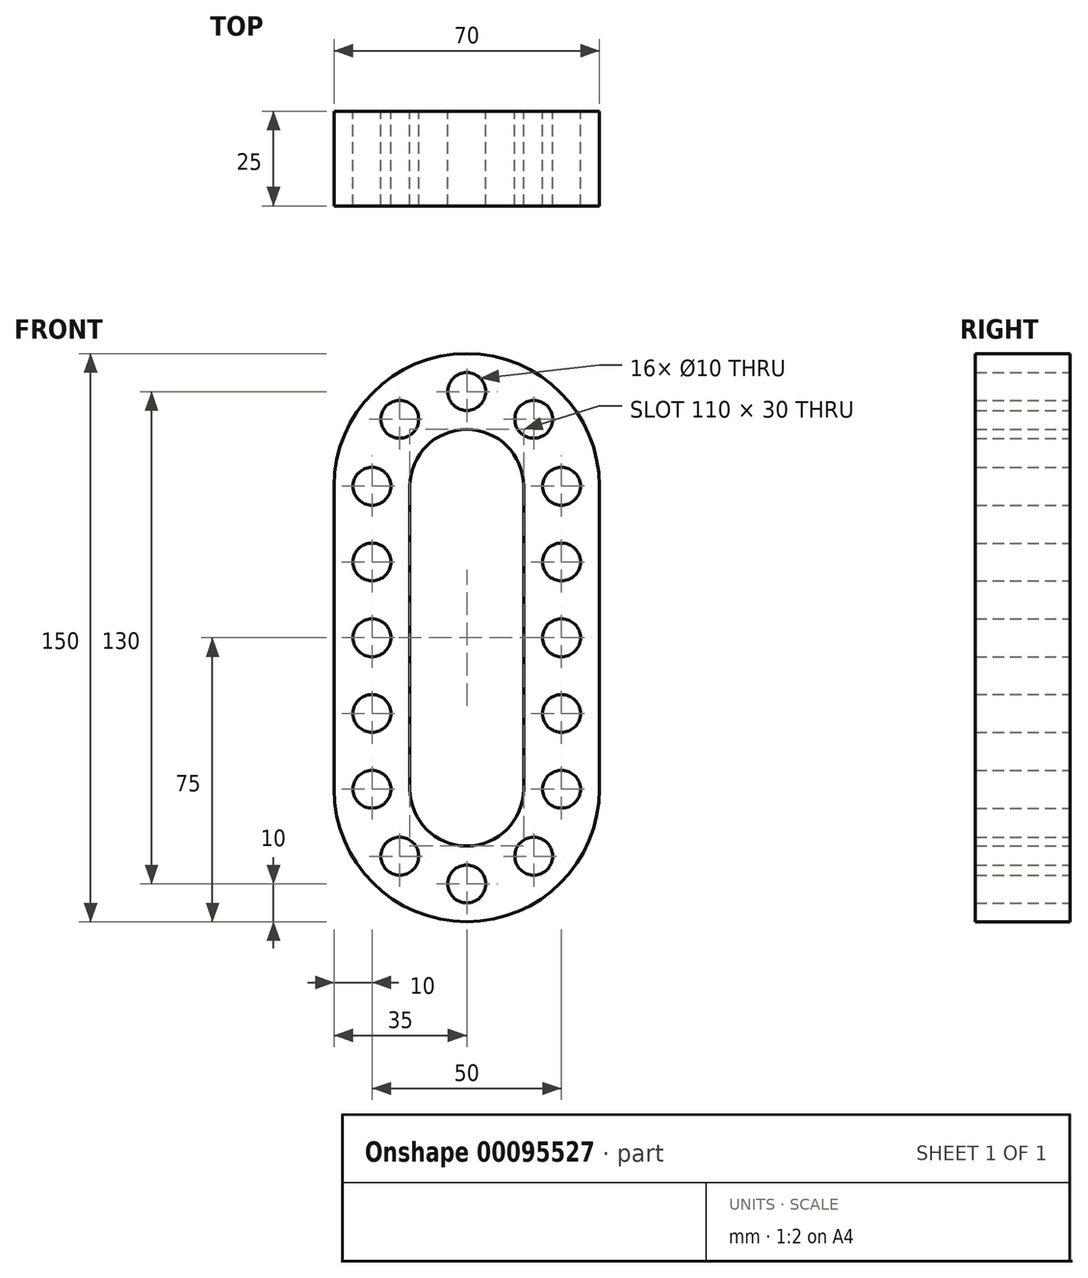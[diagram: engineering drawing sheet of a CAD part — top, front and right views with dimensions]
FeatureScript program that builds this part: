
annotation { "Feature Type Name" : "Feature", "Feature Type Description" : "" }
export const myFeature = defineFeature(function(context is Context, id is Id, definition is map)
    precondition{}
    {
        {
            var Q0;
            Q0=qCreatedBy(makeId("Front.planeOp"),FACE);
            var sketch = newSketch(context, id + "F0", { "sketchPlane" : qUnion([Q0])});
            skPoint(sketch, "E0", {"position": v(-25, 40) * mm});
            skLineSegment(sketch, "E1", {"start": v(-25, 40) * mm, "end": v(-25, 0) * mm, "construction": true});
            skArc(sketch, "E2", {"start": v(0, 65) * mm, "mid": v(-17.68, 57.68) * mm, "end": v(-25, 40) * mm, "construction": true});
            skArc(sketch, "E3.0.startCap", {"start": v(-35, 40) * mm, "mid": v(-25, 50) * mm, "end": v(-15, 40) * mm, "construction": true});
            skLineSegment(sketch, "E3.0.left", {"start": v(-15, 40) * mm, "end": v(-15, 0) * mm});
            skLineSegment(sketch, "E3.0.right", {"start": v(-35, 40) * mm, "end": v(-35, 0) * mm});
            skArc(sketch, "E3.1.startCap", {"start": v(0, 75) * mm, "mid": v(10, 65) * mm, "end": v(0, 55) * mm, "construction": true});
            skArc(sketch, "E3.1.endCap", {"start": v(-15, 40) * mm, "mid": v(-25, 30) * mm, "end": v(-35, 40) * mm, "construction": true});
            skArc(sketch, "E3.1.left", {"start": v(0, 55) * mm, "mid": v(-10.6, 50.6) * mm, "end": v(-15, 40) * mm});
            skArc(sketch, "E3.1.right", {"start": v(0, 75) * mm, "mid": v(-24.75, 64.75) * mm, "end": v(-35, 40) * mm});
            skCircle(sketch, "E4", {"center": v(-25, 40) * mm, "radius": 5 * mm});
            skCircle(sketch, "E5.1.0", {"center": v(-17.68, 57.68) * mm, "radius": 5 * mm});
            skCircle(sketch, "E5.2.0", {"center": v(0, 65) * mm, "radius": 5 * mm});
            skLineSegment(sketch, "E5.anchor1", {"start": v(0, 40) * mm, "end": v(-25, 40) * mm, "construction": true});
            skLineSegment(sketch, "E5.anchor2", {"start": v(0, 40) * mm, "end": v(0, 65) * mm, "construction": true});
            skCircle(sketch, "E6.0.1.0", {"center": v(-25, 20) * mm, "radius": 5 * mm});
            skCircle(sketch, "E6.0.2.0", {"center": v(-25, 0) * mm, "radius": 5 * mm});
            skLineSegment(sketch, "E6.direction1", {"start": v(-25, 40) * mm, "end": v(0, 40) * mm, "construction": true});
            skLineSegment(sketch, "E6.direction2", {"start": v(-25, 40) * mm, "end": v(-25, 20) * mm, "construction": true});
            skLineSegment(sketch, "E7.MirrorCS", {"start": v(0, 40) * mm, "end": v(25, 40) * mm, "construction": true});
            skArc(sketch, "E8.MirrorCS", {"start": v(15, 0) * mm, "mid": v(25, -10) * mm, "end": v(35, 0) * mm, "construction": true});
            skArc(sketch, "E9.MirrorCS", {"start": v(15, 40) * mm, "mid": v(25, 30) * mm, "end": v(35, 40) * mm, "construction": true});
            skLineSegment(sketch, "E10.MirrorCS", {"start": v(15, 40) * mm, "end": v(15, 0) * mm});
            skArc(sketch, "E11.MirrorCS", {"start": v(0, 55) * mm, "mid": v(10.6, 50.6) * mm, "end": v(15, 40) * mm});
            skLineSegment(sketch, "E12.MirrorCS", {"start": v(25, 40) * mm, "end": v(25, 20) * mm, "construction": true});
            skLineSegment(sketch, "E13.MirrorCS", {"start": v(35, 40) * mm, "end": v(35, 0) * mm});
            skArc(sketch, "E14.MirrorCS", {"start": v(35, 40) * mm, "mid": v(25, 50) * mm, "end": v(15, 40) * mm, "construction": true});
            skCircle(sketch, "E15.MirrorC", {"center": v(25, 20) * mm, "radius": 5 * mm});
            skArc(sketch, "E16.MirrorCS", {"start": v(0, 75) * mm, "mid": v(-10, 65) * mm, "end": v(0, 55) * mm, "construction": true});
            skCircle(sketch, "E17.MirrorC", {"center": v(25, 40) * mm, "radius": 5 * mm});
            skArc(sketch, "E18.MirrorCS", {"start": v(0, 75) * mm, "mid": v(24.75, 64.75) * mm, "end": v(35, 40) * mm});
            skLineSegment(sketch, "E19.MirrorCS", {"start": v(25, 40) * mm, "end": v(0, 40) * mm, "construction": true});
            skLineSegment(sketch, "E20.MirrorCS", {"start": v(25, 40) * mm, "end": v(25, 0) * mm, "construction": true});
            skCircle(sketch, "E21.MirrorC", {"center": v(17.68, 57.68) * mm, "radius": 5 * mm});
            skCircle(sketch, "E22.MirrorC", {"center": v(25, 0) * mm, "radius": 5 * mm});
            skArc(sketch, "E23.MirrorCS", {"start": v(0, 65) * mm, "mid": v(17.68, 57.68) * mm, "end": v(25, 40) * mm, "construction": true});
            skLineSegment(sketch, "E24.MirrorCS", {"start": v(-35, -40) * mm, "end": v(-35, 0) * mm});
            skArc(sketch, "E25.MirrorCS", {"start": v(0, -75) * mm, "mid": v(-24.75, -64.75) * mm, "end": v(-35, -40) * mm});
            skArc(sketch, "E26.MirrorCS", {"start": v(0, -75) * mm, "mid": v(24.75, -64.75) * mm, "end": v(35, -40) * mm});
            skLineSegment(sketch, "E27.MirrorCS", {"start": v(35, -40) * mm, "end": v(35, 0) * mm});
            skArc(sketch, "E28.MirrorCS", {"start": v(-15, 0) * mm, "mid": v(-25, -10) * mm, "end": v(-35, 0) * mm, "construction": true});
            skArc(sketch, "E29.MirrorCS", {"start": v(-15, 0) * mm, "mid": v(-25, 10) * mm, "end": v(-35, 0) * mm, "construction": true});
            skCircle(sketch, "E30.MirrorC", {"center": v(-25, -20) * mm, "radius": 5 * mm});
            skCircle(sketch, "E31.MirrorC", {"center": v(-25, -40) * mm, "radius": 5 * mm});
            skCircle(sketch, "E32.MirrorC", {"center": v(-17.68, -57.68) * mm, "radius": 5 * mm});
            skCircle(sketch, "E33.MirrorC", {"center": v(0, -65) * mm, "radius": 5 * mm});
            skCircle(sketch, "E34.MirrorC", {"center": v(25, -40) * mm, "radius": 5 * mm});
            skCircle(sketch, "E35.MirrorC", {"center": v(17.68, -57.68) * mm, "radius": 5 * mm});
            skCircle(sketch, "E36.MirrorC", {"center": v(25, -20) * mm, "radius": 5 * mm});
            skLineSegment(sketch, "E37.MirrorCS", {"start": v(-15, -40) * mm, "end": v(-15, 0) * mm});
            skArc(sketch, "E38.MirrorCS", {"start": v(0, -55) * mm, "mid": v(10.6, -50.6) * mm, "end": v(15, -40) * mm});
            skArc(sketch, "E39.MirrorCS", {"start": v(0, -55) * mm, "mid": v(-10.6, -50.6) * mm, "end": v(-15, -40) * mm});
            skLineSegment(sketch, "E40.MirrorCS", {"start": v(15, -40) * mm, "end": v(15, 0) * mm});
            skSolve(sketch);
        }
        {
            var Q0;
            Q0=makeQuery(id+"F0.imprint","IMPRINT",FACE,{"disambiguationData":[TD([[makeQuery(id+"F0.imprint","IMPRINT",EDGE,{"derivedFrom":sQuery(id+"F0.wireOp",EDGE,"E3.0.left")}),-1.0]])]});
            extrude(context, id + "F1", {"entities" : qUnion([Q0]), "depth" : 25 * mm});
        }
    });
